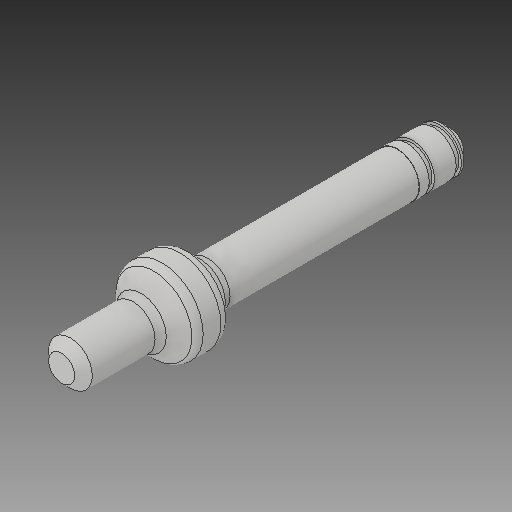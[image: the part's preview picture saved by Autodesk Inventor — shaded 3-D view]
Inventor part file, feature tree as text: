
AUTODESK INVENTOR PART (.ipt)
format: ipt  version: 2017 (Build 210142000, 142)  size: 131,072 bytes
history: native  units: in
note: dims shown in document units (in); Inventor stores cm internally (conversion verified against a paired STEP export)
features: chamfer x1
ambient origin geometry x8: Origin, YZ Plane, XZ Plane, XY Plane, X Axis, Y Axis, Z Axis, Center Point
bodies: Solid1 (feature_tree)
feature tree (1):
  chamfer  "Chamfer1"  [1 undecoded]
note: 1 required parameter value undecoded (feature->parameter linkage not recoverable at this tier; creation-order binding heuristic only, values carry confidence <= 0.55)
